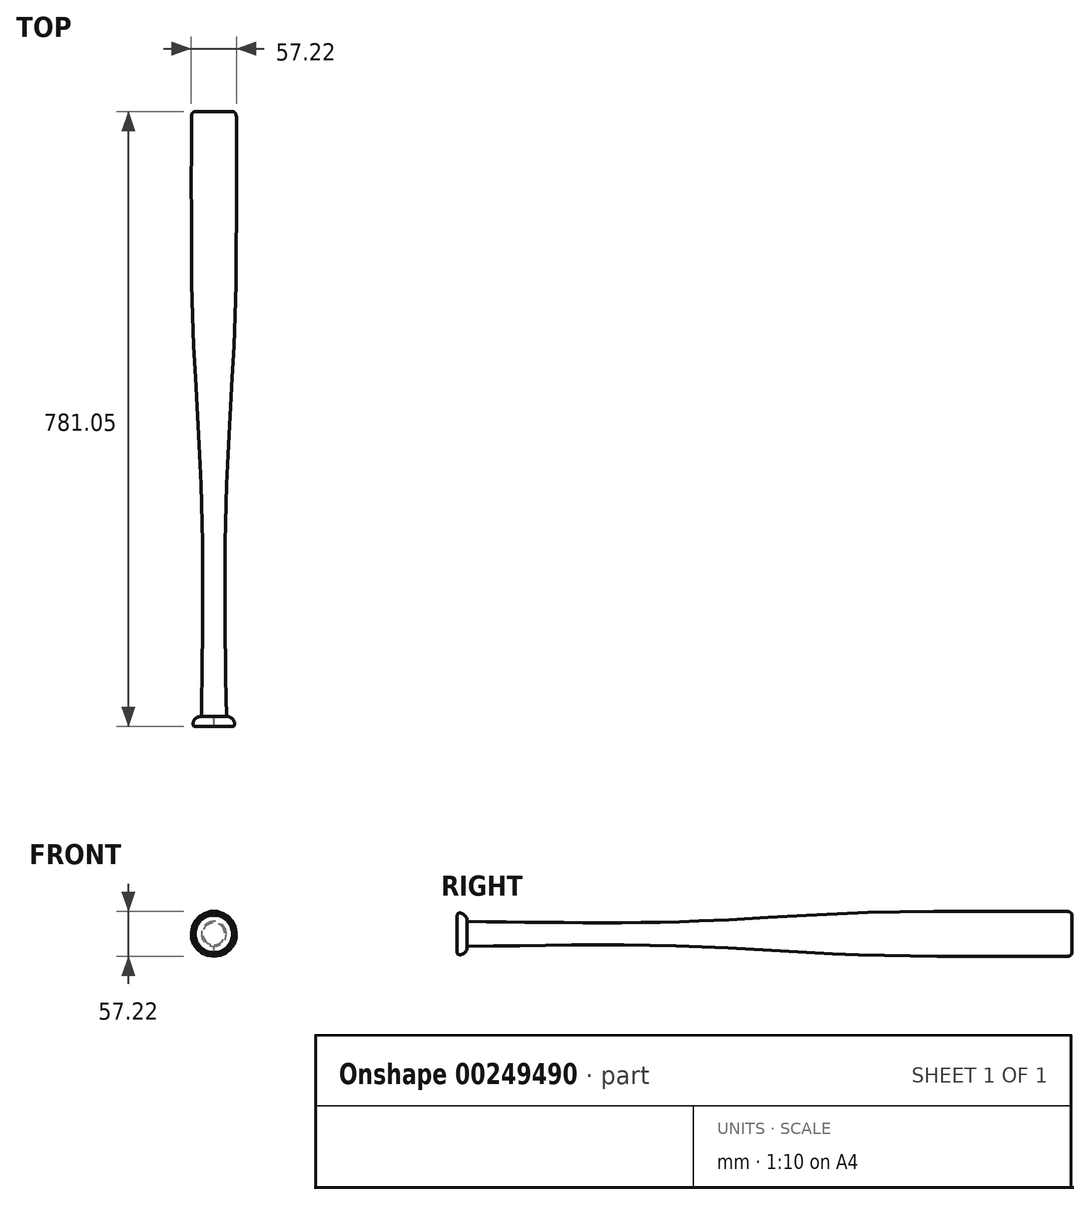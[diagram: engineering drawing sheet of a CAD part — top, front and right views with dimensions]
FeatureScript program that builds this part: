
annotation { "Feature Type Name" : "Feature", "Feature Type Description" : "" }
export const myFeature = defineFeature(function(context is Context, id is Id, definition is map)
    precondition{}
    {
        {
            var Q0;
            Q0=qCreatedBy(makeId("Front.planeOp"),FACE);
            var sketch = newSketch(context, id + "F0", { "sketchPlane" : qUnion([Q0])});
            skCircle(sketch, "E0", {"center": v(0, 0) * mm, "radius": 15.88 * mm});
            skSolve(sketch);
        }
        {
            var Q0;
            Q0=qCreatedBy(makeId("Front.planeOp"),FACE);
            cPlane(context, id + "F1", {"entities" : qUnion([Q0]), "cplaneType" : CPlaneType.OFFSET, "offset" : 127 * mm, "oppositeDirection" : true, "width" : 152.4 * mm, "height" : 152.4 * mm});
        }
        {
            var Q0;
            Q0=qCreatedBy(id+"F1.planeOp",FACE);
            var sketch = newSketch(context, id + "F2", { "sketchPlane" : qUnion([Q0])});
            skCircle(sketch, "E1", {"center": v(0, 0) * mm, "radius": 14.29 * mm});
            skSolve(sketch);
        }
        {
            var Q0;
            Q0=qCreatedBy(id+"F1.planeOp",FACE);
            cPlane(context, id + "F3", {"entities" : qUnion([Q0]), "cplaneType" : CPlaneType.OFFSET, "offset" : 127 * mm, "oppositeDirection" : true, "width" : 152.4 * mm, "height" : 152.4 * mm});
        }
        {
            var Q0;
            Q0=qCreatedBy(id+"F3.planeOp",FACE);
            var sketch = newSketch(context, id + "F4", { "sketchPlane" : qUnion([Q0])});
            skCircle(sketch, "E2", {"center": v(0, 0) * mm, "radius": 15.08 * mm});
            skSolve(sketch);
        }
        {
            var Q0;
            Q0=qCreatedBy(id+"F3.planeOp",FACE);
            cPlane(context, id + "F5", {"entities" : qUnion([Q0]), "cplaneType" : CPlaneType.OFFSET, "offset" : 127 * mm, "oppositeDirection" : true, "width" : 152.4 * mm, "height" : 152.4 * mm});
        }
        {
            var Q0;
            Q0=qCreatedBy(id+"F5.planeOp",FACE);
            var sketch = newSketch(context, id + "F6", { "sketchPlane" : qUnion([Q0])});
            skCircle(sketch, "E3", {"center": v(0, 0) * mm, "radius": 20.64 * mm});
            skSolve(sketch);
        }
        {
            var Q0;
            Q0=qCreatedBy(id+"F5.planeOp",FACE);
            cPlane(context, id + "F7", {"entities" : qUnion([Q0]), "cplaneType" : CPlaneType.OFFSET, "offset" : 127 * mm, "oppositeDirection" : true, "width" : 152.4 * mm, "height" : 152.4 * mm});
        }
        {
            var Q0;
            Q0=qCreatedBy(id+"F7.planeOp",FACE);
            var sketch = newSketch(context, id + "F8", { "sketchPlane" : qUnion([Q0])});
            skCircle(sketch, "E4", {"center": v(0, 0) * mm, "radius": 26.99 * mm});
            skSolve(sketch);
        }
        {
            var Q0;
            Q0=qCreatedBy(id+"F7.planeOp",FACE);
            cPlane(context, id + "F9", {"entities" : qUnion([Q0]), "cplaneType" : CPlaneType.OFFSET, "offset" : 127 * mm, "oppositeDirection" : true, "width" : 152.4 * mm, "height" : 152.4 * mm});
        }
        {
            var Q0;
            Q0=qCreatedBy(id+"F9.planeOp",FACE);
            var sketch = newSketch(context, id + "F10", { "sketchPlane" : qUnion([Q0])});
            skCircle(sketch, "E5", {"center": v(0, 0) * mm, "radius": 28.58 * mm});
            skSolve(sketch);
        }
        {
            var Q0;
            Q0=qCreatedBy(id+"F9.planeOp",FACE);
            cPlane(context, id + "F11", {"entities" : qUnion([Q0]), "cplaneType" : CPlaneType.OFFSET, "offset" : 127 * mm, "oppositeDirection" : true, "width" : 152.4 * mm, "height" : 152.4 * mm});
        }
        {
            var Q0;
            Q0=qCreatedBy(id+"F11.planeOp",FACE);
            var sketch = newSketch(context, id + "F12", { "sketchPlane" : qUnion([Q0])});
            skCircle(sketch, "E6", {"center": v(0, 0) * mm, "radius": 28.58 * mm});
            skSolve(sketch);
        }
        {
            var Q0;
            Q0=qCreatedBy(id+"F11.planeOp",FACE);
            cPlane(context, id + "F13", {"entities" : qUnion([Q0]), "cplaneType" : CPlaneType.OFFSET, "offset" : 6.35 * mm, "oppositeDirection" : true, "width" : 152.4 * mm, "height" : 152.4 * mm});
        }
        {
            var Q0;
            Q0=qCreatedBy(id+"F13.planeOp",FACE);
            var sketch = newSketch(context, id + "F14", { "sketchPlane" : qUnion([Q0])});
            skCircle(sketch, "E7", {"center": v(0, 0) * mm, "radius": 23.81 * mm});
            skSolve(sketch);
        }
        {
            var Q0;
            Q0=qCreatedBy(makeId("Front.planeOp"),FACE);
            cPlane(context, id + "F15", {"entities" : qUnion([Q0]), "cplaneType" : CPlaneType.OFFSET, "offset" : 12.7 * mm, "width" : 152.4 * mm, "height" : 152.4 * mm});
        }
        {
            var Q0;
            Q0=qCreatedBy(id+"F15.planeOp",FACE);
            var sketch = newSketch(context, id + "F16", { "sketchPlane" : qUnion([Q0])});
            skCircle(sketch, "E8", {"center": v(0, 0) * mm, "radius": 23.81 * mm});
            skSolve(sketch);
        }
        {
            var Q0;
            Q0=makeQuery(id+"F0.imprint","IMPRINT",FACE,{"disambiguationData":[TD([[makeQuery(id+"F0.imprint","IMPRINT",EDGE,{"derivedFrom":sQuery(id+"F0.wireOp",EDGE,"E0")}),1.0]])]});
            var Q1;
            Q1=makeQuery(id+"F2.imprint","IMPRINT",FACE,{"disambiguationData":[TD([[makeQuery(id+"F2.imprint","IMPRINT",EDGE,{"derivedFrom":sQuery(id+"F2.wireOp",EDGE,"E1")}),1.0]])]});
            var Q2;
            Q2=makeQuery(id+"F4.imprint","IMPRINT",FACE,{"disambiguationData":[TD([[makeQuery(id+"F4.imprint","IMPRINT",EDGE,{"derivedFrom":sQuery(id+"F4.wireOp",EDGE,"E2")}),1.0]])]});
            var Q3;
            Q3=makeQuery(id+"F6.imprint","IMPRINT",FACE,{"disambiguationData":[TD([[makeQuery(id+"F6.imprint","IMPRINT",EDGE,{"derivedFrom":sQuery(id+"F6.wireOp",EDGE,"E3")}),1.0]])]});
            var Q4;
            Q4=makeQuery(id+"F8.imprint","IMPRINT",FACE,{"disambiguationData":[TD([[makeQuery(id+"F8.imprint","IMPRINT",EDGE,{"derivedFrom":sQuery(id+"F8.wireOp",EDGE,"E4")}),1.0]])]});
            var Q5;
            Q5=makeQuery(id+"F10.imprint","IMPRINT",FACE,{"disambiguationData":[TD([[makeQuery(id+"F10.imprint","IMPRINT",EDGE,{"derivedFrom":sQuery(id+"F10.wireOp",EDGE,"E5")}),1.0]])]});
            var Q6;
            Q6=makeQuery(id+"F12.imprint","IMPRINT",FACE,{"disambiguationData":[TD([[makeQuery(id+"F12.imprint","IMPRINT",EDGE,{"derivedFrom":sQuery(id+"F12.wireOp",EDGE,"E6")}),1.0]])]});
            loft(context, id + "F17", {"sheetProfilesArray" : [{ "sheetProfileEntities" : qUnion([Q0]) }, { "sheetProfileEntities" : qUnion([Q1]) }, { "sheetProfileEntities" : qUnion([Q2]) }, { "sheetProfileEntities" : qUnion([Q3]) }, { "sheetProfileEntities" : qUnion([Q4]) }, { "sheetProfileEntities" : qUnion([Q5]) }, { "sheetProfileEntities" : qUnion([Q6]) }]});
        }
        {
            var Q1;
            Q1=makeQuery(id+"F16.imprint","IMPRINT",FACE,{"disambiguationData":[TD([[makeQuery(id+"F16.imprint","IMPRINT",EDGE,{"derivedFrom":sQuery(id+"F16.wireOp",EDGE,"E8")}),1.0]])]});
            var Q2;
            Q2=makeQuery(id+"F17.opLoft","CAP_FACE",FACE,{"disambiguationData":[OSD([makeQuery(id+"F0.imprint","IMPRINT",FACE,{"disambiguationData":[TD([[makeQuery(id+"F0.imprint","IMPRINT",EDGE,{"derivedFrom":sQuery(id+"F0.wireOp",EDGE,"E0")}),1.0]])]})])],"isStart":true});
            loft(context, id + "F18", {"operationType" : NewBodyOperationType.ADD, "startCondition" : LoftEndDerivativeType.TANGENT_TO_PROFILE, "startMagnitude" : -2, "endCondition" : LoftEndDerivativeType.TANGENT_TO_PROFILE, "endMagnitude" : 4, "sheetProfilesArray" : [{ "sheetProfileEntities" : qUnion([Q1]) }, { "sheetProfileEntities" : qUnion([Q2]) }]});
        }
        {
            var Q1;
            Q1=makeQuery(id+"F17.opLoft","CAP_FACE",FACE,{"disambiguationData":[OSD([makeQuery(id+"F12.imprint","IMPRINT",FACE,{"disambiguationData":[TD([[makeQuery(id+"F12.imprint","IMPRINT",EDGE,{"derivedFrom":sQuery(id+"F12.wireOp",EDGE,"E6")}),1.0]])]})])],"isStart":true});
            var Q2;
            Q2=makeQuery(id+"F14.imprint","IMPRINT",FACE,{"disambiguationData":[TD([[makeQuery(id+"F14.imprint","IMPRINT",EDGE,{"derivedFrom":sQuery(id+"F14.wireOp",EDGE,"E7")}),1.0]])]});
            loft(context, id + "F19", {"operationType" : NewBodyOperationType.ADD, "startCondition" : LoftEndDerivativeType.NORMAL_TO_PROFILE, "startMagnitude" : 1, "endCondition" : LoftEndDerivativeType.TANGENT_TO_PROFILE, "endMagnitude" : 2, "sheetProfilesArray" : [{ "sheetProfileEntities" : qUnion([Q1]) }, { "sheetProfileEntities" : qUnion([Q2]) }]});
        }
    });
